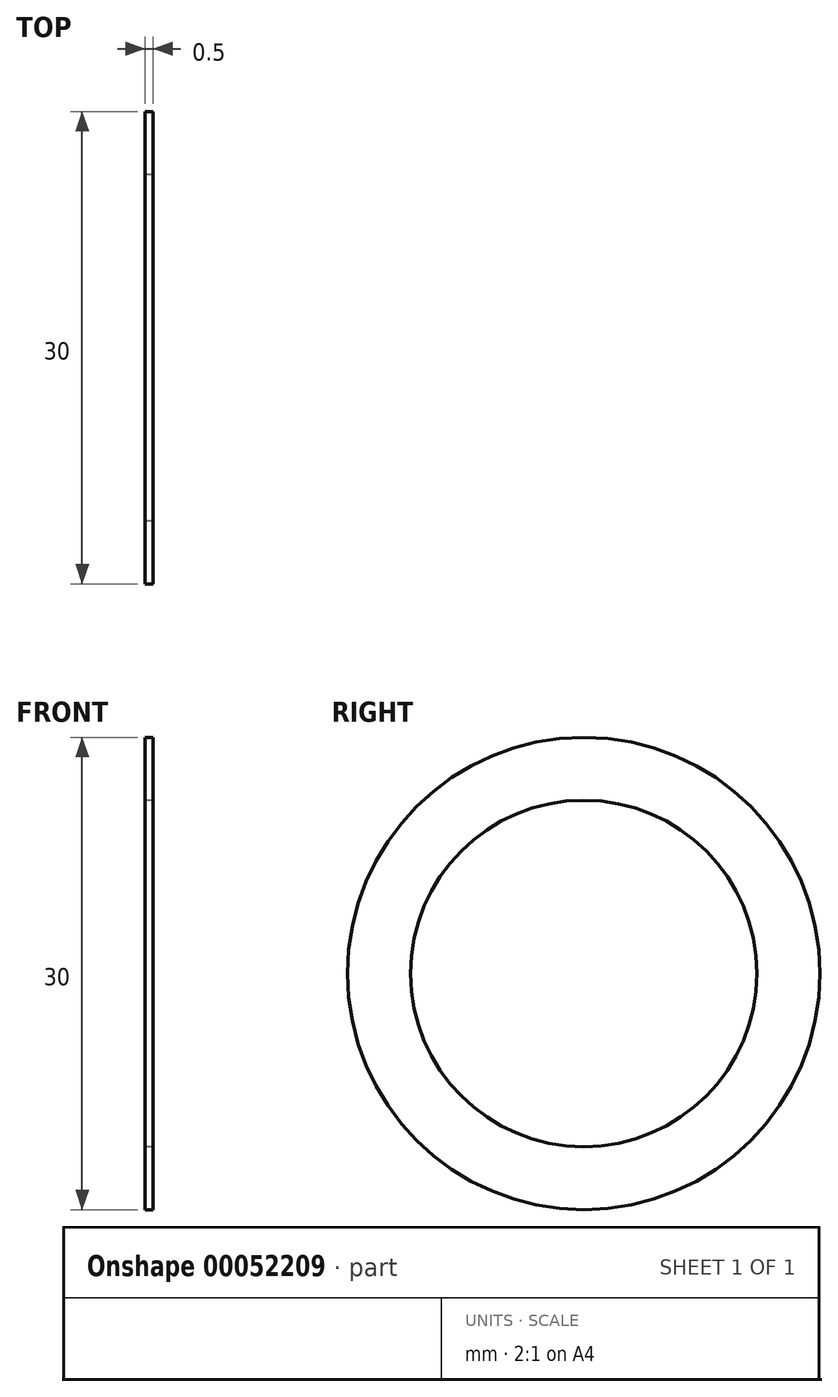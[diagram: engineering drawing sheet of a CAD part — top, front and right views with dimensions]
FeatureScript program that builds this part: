
annotation { "Feature Type Name" : "Feature", "Feature Type Description" : "" }
export const myFeature = defineFeature(function(context is Context, id is Id, definition is map)
    precondition{}
    {
        {
            var Q0;
            Q0=qCreatedBy(makeId("Top.planeOp"),FACE);
            var sketch = newSketch(context, id + "F0", { "sketchPlane" : qUnion([Q0])});
            skLineSegment(sketch, "E0.bottom", {"start": v(0, 15) * mm, "end": v(0.5, 15) * mm});
            skLineSegment(sketch, "E0.top", {"start": v(0, 11) * mm, "end": v(0.5, 11) * mm});
            skLineSegment(sketch, "E0.left", {"start": v(0, 15) * mm, "end": v(0, 11) * mm});
            skLineSegment(sketch, "E0.right", {"start": v(0.5, 15) * mm, "end": v(0.5, 11) * mm});
            skLineSegment(sketch, "E1", {"start": v(-15.04, 0) * mm, "end": v(34.3, 0) * mm, "construction": true});
            skSolve(sketch);
        }
        {
            var Q0;
            Q0=makeQuery(id+"F0.imprint","IMPRINT",FACE,{"disambiguationData":[TD([[makeQuery(id+"F0.imprint","IMPRINT",EDGE,{"derivedFrom":sQuery(id+"F0.wireOp",EDGE,"E0.bottom")}),-1.0]])]});
            var Q1;
            Q1=sQuery(id+"F0.wireOp",EDGE,"E1");
            revolve(context, id + "F1", {"entities" : qUnion([Q0]), "axis" : qUnion([Q1]), "revolveType" : RevolveType.FULL});
        }
    });
